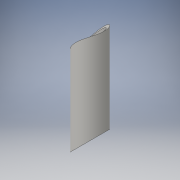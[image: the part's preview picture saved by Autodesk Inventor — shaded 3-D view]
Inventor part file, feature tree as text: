
AUTODESK INVENTOR PART (.ipt)
format: ipt  version: 2016 (Build 200138000, 138)  size: 150,016 bytes
history: native  units: in
note: dims shown in document units (in); Inventor stores cm internally (conversion verified against a paired STEP export)
features: plane x9, extrude x7, sketch x7
ambient origin geometry x8: Origin, YZ Plane, XZ Plane, XY Plane, X Axis, Y Axis, Z Axis, Center Point
bodies: Solid1 (feature_tree)
feature tree (23):
  extrude  "Extrusion1"  Depth=1.913in
  plane  "Work Plane4"
  extrude  "Extrusion2"  Depth=3.0in
  extrude  "Extrusion3"  Depth=2.248in
  extrude  "Extrusion4"  Depth=2.248in
  extrude  "Extrusion5"  Depth=2.5in TaperAngle=0.0deg
  plane  "Work Plane5"
  plane  "Work Plane6"
  plane  "Work Plane9"
  extrude  "Extrusion6"  Depth=0.5in TaperAngle=0.0deg
  extrude  "Extrusion7"  Depth=2.0in TaperAngle=0.0deg
  sketch  "Sketch1"  dims[d0=1.58in d1=1.913in]
  plane  "Work Plane1"
  plane  "Work Plane2"
  plane  "Work Plane3"
  sketch  "Sketch2"  dims[d2=6.0in d3=0.0in d4=3.0in]
  sketch  "Sketch3"  dims[d5=0.84in d6=2.248in]
  sketch  "Sketch4"  dims[d7=2.248in d8=4.496in]
  sketch  "Sketch5"  dims[d9=6.0in d10=0.0in d11=2.5in d12=0.0in]
  plane  "Work Plane7"
  plane  "Work Plane8"
  sketch  "Sketch6"  dims[d13=2.0in d14=0.0in d15=0.5in d16=0.0in]
  sketch  "Sketch7"  dims[d17=-0.676in d18=1.352in d19=2.0in d20=0.0in d21=2.0in d22=0.0in]
